# Revit family: Gira_5333100
name_source: partatom
category: Elektroinstallationen
revit_build: Autodesk Revit 2017 (Build: 20160225_1515(x64)
units: mm (PartAtom-declared; Revit-internal decimal feet)

## family parameters
Basisbauteil = Fläche
Beim Laden mit Abzugskörper schneiden = Nein
Bemaßung runder Anschluss = Durchmesser verwenden
Beschriftungsausrichtung beibehalten = Nein
Gemeinsam genutzt = Nein
Raumberechnungspunkt = Nein
Teiletyp = Normal

## types (1)
- Gira_5333100
    BIM = https://media.stage.bim.site und Tasten.rfa
    Beschreibung = eNet wall tr.in.sp.3g Sys55 ClPw,eNet wireless wall transmitter, 3-gang,System 55, rockers with inscription space,clear + pure white glossy,Features:,- The eNet wireless transmitters transfer switching, dimming, and blind adjustment commands to corresponding eNet wireless receivers.,- Simple extension of existing switch combinations.,- The installation can be carried out without a surface-mounted housing or device box.,- The wireless wall transmitter can be attached to walls with screws or glued onto smooth or transparent surfaces with the mounting plate.,- Transmission of switching, dimming, blind adjustment, and scene commands.,- Switchover function, optimised for the control of momentary-contact actuators.,- Rocker can be set as channel or scene function.,- Two-colour LEDs on the right and left of the buttons for signalling.,- Battery-operated device.,Can be set with eNet server::,- Fully encrypted wireless transmission (AES CCM) from eNet Server software version 2.0.,- Signalling of the transmission status deactivatable.,- Operation locks.,- All-On or All-Off scenes, threshold value scenes, and individual scenes can be configured.,- Configuration of scene button via eNet SMART HOME app (if-then rules) to trigger actions, scenes, or timers.,- Device software update.,- Localisation of the device.,,Notes :,- Batteries are consumables and must be replaced regularly. Please observe the regulations on the disposal of used batteries.,- The wireless wall transmitter is supplied with a program-neutral start-up rocker. The suitable rocker set for the design line must be ordered separately.,- The range can be reduced when using metal rocker sets and or metal cover frames.
    Bus connection included = Nein
    Bus system KNX = Nein
    Bus system KNX radio = Nein
    Bus system LON = Nein
    Bus system Powernet = Nein
    Bus system radio frequent = Ja
    Colour = White
    Data sheet = https://katalog.gira.de
    GTIN = 4010337116547
    HAN = 5333100
    Hersteller = Gira
    Material = Other
    Material quality = Other
    Model = Wall-mounted transmitter complete
    Mounting method = Surface mounted (plaster)
    Number of channels = 3
    Other bus systems = None
    Productwebsite = http://katalog.gira.de
    RAL-number (akin) = 9010
    Surface finishing = Glossy
    Surface protection = Other
    Transparent = Nein
    Typname = Gira eNet WL wall transm. 3-g in.sp. System 55 clear/p.white
    URL = https://www.gira.de
    Vorgabe-Ansicht = 1219 mm

## geometry (parser evidence)
native form markers: Sweep x7
no freeform markers — native parametric forms only
